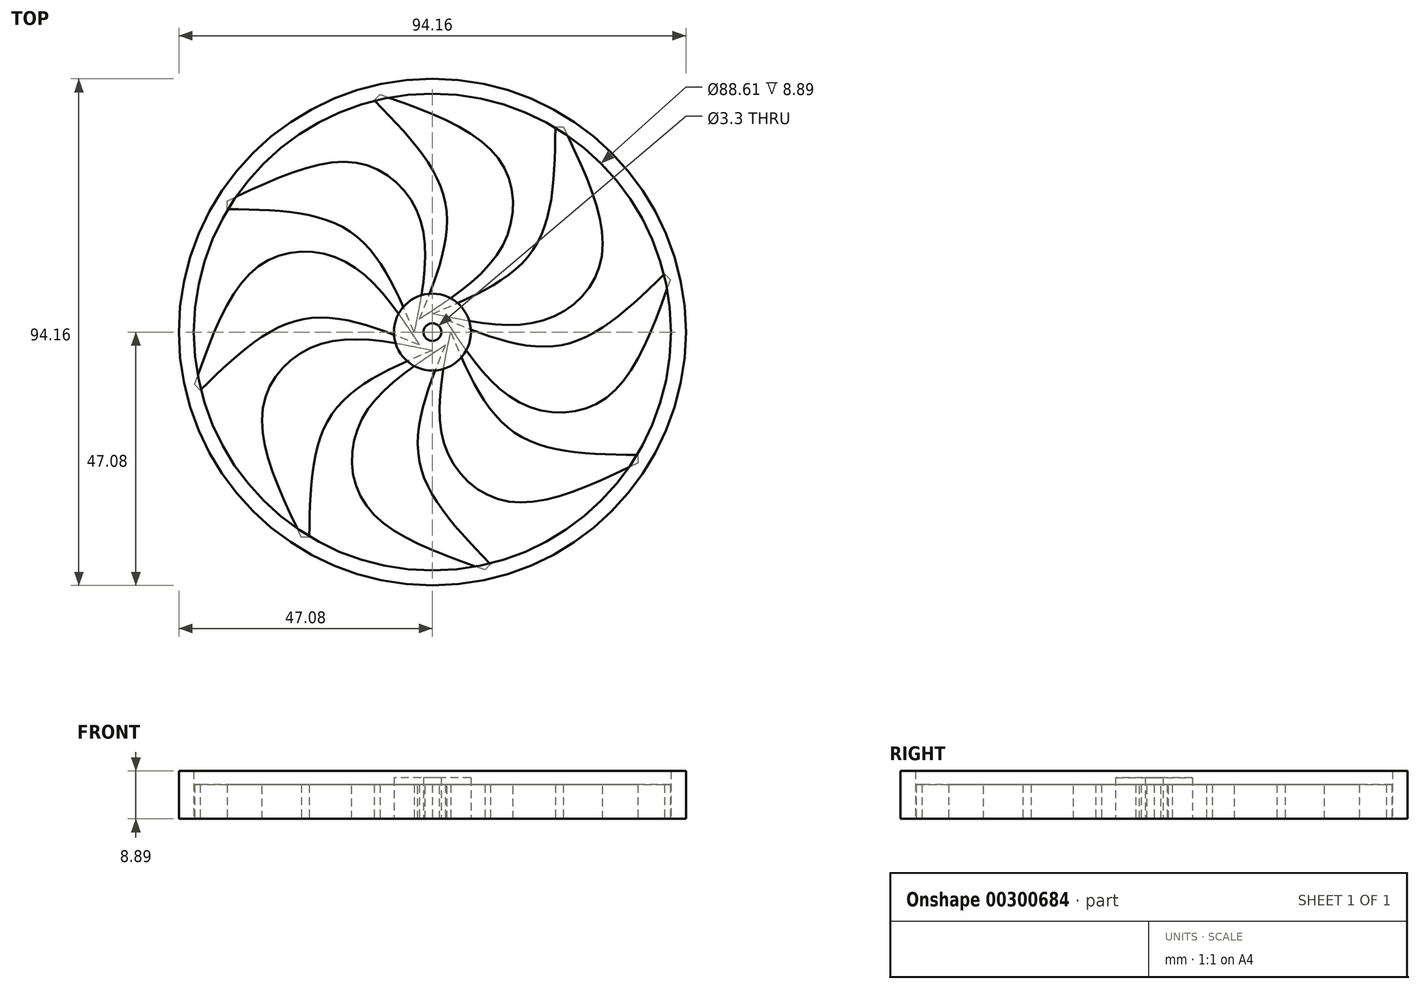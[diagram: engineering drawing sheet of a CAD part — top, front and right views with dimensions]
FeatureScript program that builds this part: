
annotation { "Feature Type Name" : "Feature", "Feature Type Description" : "" }
export const myFeature = defineFeature(function(context is Context, id is Id, definition is map)
    precondition{}
    {
        {
            var Q0;
            Q0=qCreatedBy(makeId("Top.planeOp"),FACE);
            var sketch = newSketch(context, id + "F0", { "sketchPlane" : qUnion([Q0])});
            skFitSpline(sketch, "E0", {"points": [v(0, 3.4) * mm, v(18.74, 15.35) * mm, v(22.84, 38.13) * mm], "startDerivative": vector(45.21, 18.96) * mm, "endDerivative": vector(0.63, 50.4) * mm});
            skFitSpline(sketch, "E1", {"points": [v(24.34, 38.13) * mm, v(31.43, 13.85) * mm, v(20.98, 2.28) * mm, v(0, 3.4) * mm], "startDerivative": vector(33.6, -70.11) * mm, "endDerivative": vector(-66.05, 13.9) * mm});
            skLineSegment(sketch, "E2", {"start": v(22.84, 38.13) * mm, "end": v(24.34, 38.13) * mm});
            skSolve(sketch);
        }
        {
            var Q0;
            Q0 = qSketchRegion(id + "F0", true);
            extrude(context, id + "F1", {"entities" : qUnion([Q0]), "depth" : 6.35 * mm});
        }
        {
            var Q0;
            Q0=qCreatedBy(makeId("Front.planeOp"),FACE);
            var sketch = newSketch(context, id + "F2", { "sketchPlane" : qUnion([Q0])});
            skLineSegment(sketch, "E3", {"start": v(0, 0) * mm, "end": v(0, 46.5) * mm, "construction": true});
            skSolve(sketch);
        }
        {
            var Q0;
            Q0=makeQuery(id+"F1.opExtrude","SWEPT_BODY",BODY,{"disambiguationData":[OSD([sQuery(id+"F0.wireOp",EDGE,"E0"),sQuery(id+"F0.wireOp",EDGE,"E1"),sQuery(id+"F0.wireOp",EDGE,"E2")])]});
            var Q1;
            Q1=sQuery(id+"F2.wireOp",EDGE,"E3");
            circularPattern(context, id + "F3", {"entities" : qUnion([Q0]), "axis" : qUnion([Q1]), "angle" : 360 * degree, "instanceCount" : 8, "equalSpace" : true});
        }
        {
            var Q0;
            Q0=qCreatedBy(makeId("Top.planeOp"),FACE);
            var sketch = newSketch(context, id + "F4", { "sketchPlane" : qUnion([Q0])});
            skCircle(sketch, "E4", {"center": v(0, 0) * mm, "radius": 44.3 * mm});
            skCircle(sketch, "E5", {"center": v(0, 0) * mm, "radius": 47.08 * mm});
            skSolve(sketch);
        }
        {
            var Q0;
            Q0 = qSketchRegion(id + "F4", true);
            extrude(context, id + "F5", {"entities" : qUnion([Q0]), "depth" : 8.9 * mm});
        }
        {
            var Q0;
            Q0=qCreatedBy(makeId("Top.planeOp"),FACE);
            var sketch = newSketch(context, id + "F6", { "sketchPlane" : qUnion([Q0])});
            skCircle(sketch, "E6", {"center": v(0, 0) * mm, "radius": 7.14 * mm});
            skCircle(sketch, "E7", {"center": v(0, 0) * mm, "radius": 1.65 * mm});
            skSolve(sketch);
        }
        {
            var Q0;
            Q0 = qSketchRegion(id + "F6", true);
            extrude(context, id + "F7", {"entities" : qUnion([Q0]), "depth" : 7.62 * mm});
        }
    });
